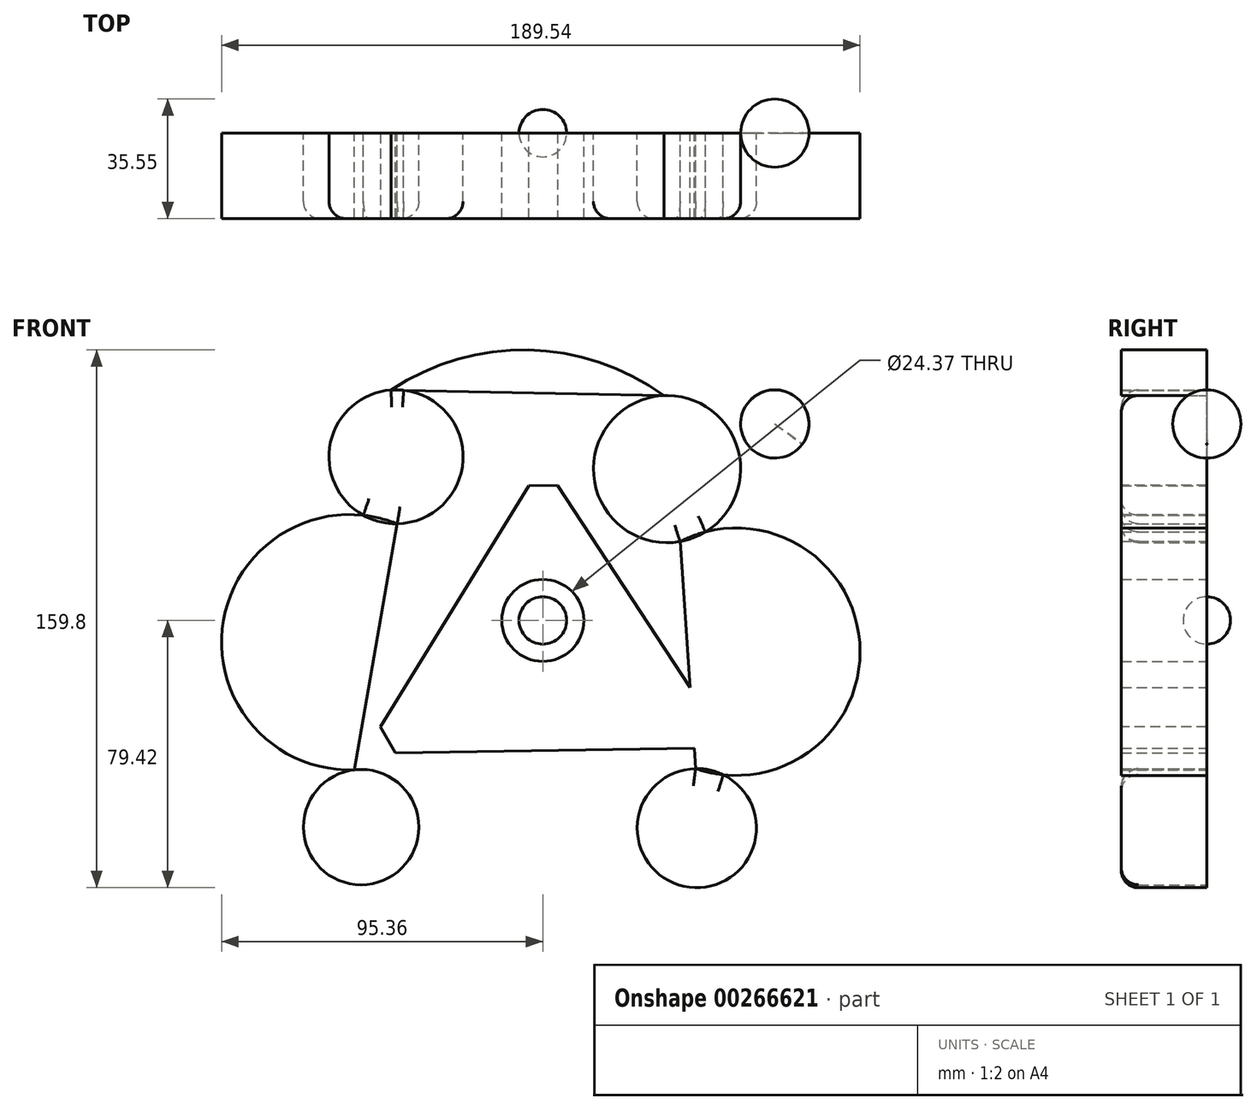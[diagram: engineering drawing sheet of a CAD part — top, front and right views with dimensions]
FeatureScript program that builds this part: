
annotation { "Feature Type Name" : "Feature", "Feature Type Description" : "" }
export const myFeature = defineFeature(function(context is Context, id is Id, definition is map)
    precondition{}
    {
        {
            var Q0;
            Q0=qCreatedBy(makeId("Front.planeOp"),FACE);
            var sketch = newSketch(context, id + "F0", { "sketchPlane" : qUnion([Q0])});
            skLineSegment(sketch, "E0", {"start": v(-53.05, -39.5) * mm, "end": v(0, 46.78) * mm});
            skLineSegment(sketch, "E1", {"start": v(0, 46.78) * mm, "end": v(55.38, -37.75) * mm});
            skLineSegment(sketch, "E2", {"start": v(-53.05, -39.5) * mm, "end": v(55.38, -37.75) * mm});
            skCircle(sketch, "E3", {"center": v(0, 0) * mm, "radius": 12.18 * mm});
            skSolve(sketch);
        }
        {
            var Q0;
            Q0=makeQuery(id+"F0.imprint","IMPRINT",FACE,{"disambiguationData":[TD([[makeQuery(id+"F0.imprint","IMPRINT",EDGE,{"derivedFrom":sQuery(id+"F0.wireOp",EDGE,"E0")}),-1.0]])]});
            extrude(context, id + "F1", {"entities" : qUnion([Q0]), "depth" : 25.4 * mm});
        }
        {
            var Q0;
            Q0=makeQuery(id+"F1.opExtrude","SWEPT_EDGE",EDGE,{"disambiguationData":[OSD([sQuery(id+"F0.wireOp",EDGE,"E0"),sQuery(id+"F0.wireOp",EDGE,"E1")])]});
            var Q1;
            Q1=makeQuery(id+"F1.opExtrude","SWEPT_EDGE",EDGE,{"disambiguationData":[OSD([sQuery(id+"F0.wireOp",EDGE,"E1"),sQuery(id+"F0.wireOp",EDGE,"E2")])]});
            var Q2;
            Q2=makeQuery(id+"F1.opExtrude","SWEPT_EDGE",EDGE,{"disambiguationData":[OSD([sQuery(id+"F0.wireOp",EDGE,"E0"),sQuery(id+"F0.wireOp",EDGE,"E2")])]});
            chamfer(context, id + "F2", {"entities" : qUnion([Q0, Q1, Q2]), "width" : 5.08 * mm, "tangentPropagation" : true});
        }
        {
            var Q0;
            Q0=qCreatedBy(makeId("Front.planeOp"),FACE);
            var sketch = newSketch(context, id + "F3", { "sketchPlane" : qUnion([Q0])});
            skCircle(sketch, "E4", {"center": v(-43.59, 48.62) * mm, "radius": 19.9 * mm});
            skCircle(sketch, "E5", {"center": v(36.88, 44.96) * mm, "radius": 21.85 * mm});
            skCircle(sketch, "E6", {"center": v(-53.95, -61.42) * mm, "radius": 17.14 * mm});
            skCircle(sketch, "E7", {"center": v(45.72, -61.72) * mm, "radius": 17.7 * mm});
            skArc(sketch, "E8", {"start": v(35.96, 66.8) * mm, "mid": v(-4.28, 80.37) * mm, "end": v(-45.04, 68.47) * mm});
            skArc(sketch, "E9", {"start": v(-43.25, 28.72) * mm, "mid": v(-94.8, 0.05) * mm, "end": v(-56.04, -44.4) * mm});
            skArc(sketch, "E10", {"start": v(45.4, -44.03) * mm, "mid": v(94.1, -6.78) * mm, "end": v(40.75, 23.45) * mm});
            skLineSegment(sketch, "E11", {"start": v(-56.04, -44.4) * mm, "end": v(-43.25, 28.72) * mm});
            skLineSegment(sketch, "E12", {"start": v(-45.04, 68.47) * mm, "end": v(35.96, 66.8) * mm});
            skLineSegment(sketch, "E13", {"start": v(40.75, 23.45) * mm, "end": v(45.4, -44.03) * mm});
            skSolve(sketch);
        }
        {
            var Q0;
            Q0=makeQuery(id+"F3.imprint","IMPRINT",FACE,{"disambiguationData":[TD([[makeQuery(id+"F3.imprint","IMPRINT",EDGE,{"derivedFrom":sQuery(id+"F3.wireOp",EDGE,"E6")}),1.0]])]});
            var Q1;
            {var subQ0=sQuery(id+"F3.wireOp",EDGE,"E11");Q1=makeQuery(id+"F3.imprint","IMPRINT",FACE,{"disambiguationData":[TD([[makeQuery(id+"F3.imprint","IMPRINT",EDGE,{"derivedFrom":subQ0}),1.0]])]});}
            var Q2;
            {var subQ1=sQuery(id+"F3.wireOp",EDGE,"E4");var subQ3=sQuery(id+"F3.wireOp",EDGE,"E9");var subQ4=makeQuery(id+"F3.imprint","INTERSECT",VERTEX,{"derivedFrom":[subQ1,subQ3]});Q2=makeQuery(id+"F3.imprint","IMPRINT",FACE,{"disambiguationData":[TD([[makeQuery(id+"F3.imprint","IMPRINT",EDGE,{"disambiguationData":[TD([[subQ4,1.0]])],"derivedFrom":subQ1}),1.0]])]});}
            var Q3;
            {var subQ1=sQuery(id+"F3.wireOp",EDGE,"E8");Q3=makeQuery(id+"F3.imprint","IMPRINT",FACE,{"disambiguationData":[TD([[makeQuery(id+"F3.imprint","IMPRINT",EDGE,{"derivedFrom":subQ1}),1.0]])]});}
            var Q4;
            {var subQ0=sQuery(id+"F3.wireOp",EDGE,"E5");var subQ2=sQuery(id+"F3.wireOp",EDGE,"E10");var subQ4=makeQuery(id+"F3.imprint","INTERSECT",VERTEX,{"derivedFrom":[subQ0,subQ2]});Q4=makeQuery(id+"F3.imprint","IMPRINT",FACE,{"disambiguationData":[TD([[makeQuery(id+"F3.imprint","IMPRINT",EDGE,{"disambiguationData":[TD([[subQ4,-1.0]])],"derivedFrom":subQ0}),1.0]])]});}
            var Q5;
            {var subQ0=sQuery(id+"F3.wireOp",EDGE,"E13");Q5=makeQuery(id+"F3.imprint","IMPRINT",FACE,{"disambiguationData":[TD([[makeQuery(id+"F3.imprint","IMPRINT",EDGE,{"derivedFrom":subQ0}),1.0]])]});}
            var Q6;
            {var subQ0=sQuery(id+"F3.wireOp",EDGE,"E10");var subQ1=sQuery(id+"F3.wireOp",EDGE,"E7");var subQ3=makeQuery(id+"F3.imprint","INTERSECT",VERTEX,{"derivedFrom":[subQ1,subQ0]});Q6=makeQuery(id+"F3.imprint","IMPRINT",FACE,{"disambiguationData":[TD([[makeQuery(id+"F3.imprint","IMPRINT",EDGE,{"disambiguationData":[TD([[subQ3,1.0]])],"derivedFrom":subQ1}),1.0]])]});}
            extrude(context, id + "F4", {"entities" : qUnion([Q0, Q1, Q2, Q3, Q4, Q5, Q6]), "operationType" : NewBodyOperationType.ADD, "depth" : 25.4 * mm});
        }
        {
            var Q0;
            Q0=qCreatedBy(makeId("Front.planeOp"),FACE);
            var sketch = newSketch(context, id + "F5", { "sketchPlane" : qUnion([Q0])});
            skCircle(sketch, "E14", {"center": v(68.88, 58.37) * mm, "radius": 10.15 * mm});
            skLineSegment(sketch, "E15", {"start": v(57.6, 66.6) * mm, "end": v(68.88, 58.37) * mm});
            skLineSegment(sketch, "E16", {"start": v(68.88, 58.37) * mm, "end": v(83.82, 47.7) * mm});
            skSolve(sketch);
        }
        {
            var Q0;
            {var subQ0=sQuery(id+"F5.wireOp",EDGE,"E15");var subQ1=sQuery(id+"F5.wireOp",EDGE,"E14");var subQ2=makeQuery(id+"F5.imprint","INTERSECT",VERTEX,{"derivedFrom":[subQ1,subQ0]});Q0=makeQuery(id+"F5.imprint","IMPRINT",FACE,{"disambiguationData":[TD([[makeQuery(id+"F5.imprint","IMPRINT",EDGE,{"disambiguationData":[TD([[subQ2,1.0]])],"derivedFrom":subQ1}),1.0]])]});}
            var Q1;
            Q1=sQuery(id+"F5.wireOp",EDGE,"E15");
            revolve(context, id + "F6", {"entities" : qUnion([Q0]), "axis" : qUnion([Q1]), "revolveType" : RevolveType.FULL});
        }
        {
            var Q0;
            Q0=qCreatedBy(makeId("Front.planeOp"),FACE);
            var sketch = newSketch(context, id + "F7", { "sketchPlane" : qUnion([Q0])});
            skCircle(sketch, "E17", {"center": v(0, 0) * mm, "radius": 7.05 * mm});
            skLineSegment(sketch, "E18", {"start": v(0, 7.05) * mm, "end": v(0, -7.05) * mm});
            skSolve(sketch);
        }
        {
            var Q0;
            {var subQ0=sQuery(id+"F7.wireOp",EDGE,"E18");Q0=makeQuery(id+"F7.imprint","IMPRINT",FACE,{"disambiguationData":[TD([[makeQuery(id+"F7.imprint","IMPRINT",EDGE,{"derivedFrom":subQ0}),-1.0]])]});}
            var Q1;
            Q1=sQuery(id+"F7.wireOp",EDGE,"E18");
            revolve(context, id + "F8", {"entities" : qUnion([Q0]), "axis" : qUnion([Q1]), "revolveType" : RevolveType.FULL});
        }
        {
            var Q0;
            Q0=makeQuery(id+"F4.opExtrude","CAP_FACE",FACE,{"disambiguationData":[OSD([sQuery(id+"F3.wireOp",EDGE,"E4"),sQuery(id+"F3.wireOp",EDGE,"E9"),sQuery(id+"F3.wireOp",EDGE,"E12")])],"isStart":false});
            var Q1;
            Q1=makeQuery(id+"F4.opExtrude","CAP_FACE",FACE,{"disambiguationData":[OSD([sQuery(id+"F3.wireOp",EDGE,"E6")])],"isStart":false});
            var Q2;
            Q2=makeQuery(id+"F4.opExtrude","CAP_FACE",FACE,{"disambiguationData":[OSD([sQuery(id+"F3.wireOp",EDGE,"E7"),sQuery(id+"F3.wireOp",EDGE,"E10")])],"isStart":false});
            var Q3;
            Q3=makeQuery(id+"F4.opExtrude","CAP_FACE",FACE,{"disambiguationData":[OSD([sQuery(id+"F3.wireOp",EDGE,"E5"),sQuery(id+"F3.wireOp",EDGE,"E10")])],"isStart":false});
            fillet(context, id + "F9", {"entities" : qUnion([Q0, Q1, Q2, Q3]), "radius" : 5.08 * mm, "tangentPropagation" : true, "allowEdgeOverflow" : false});
        }
    });
